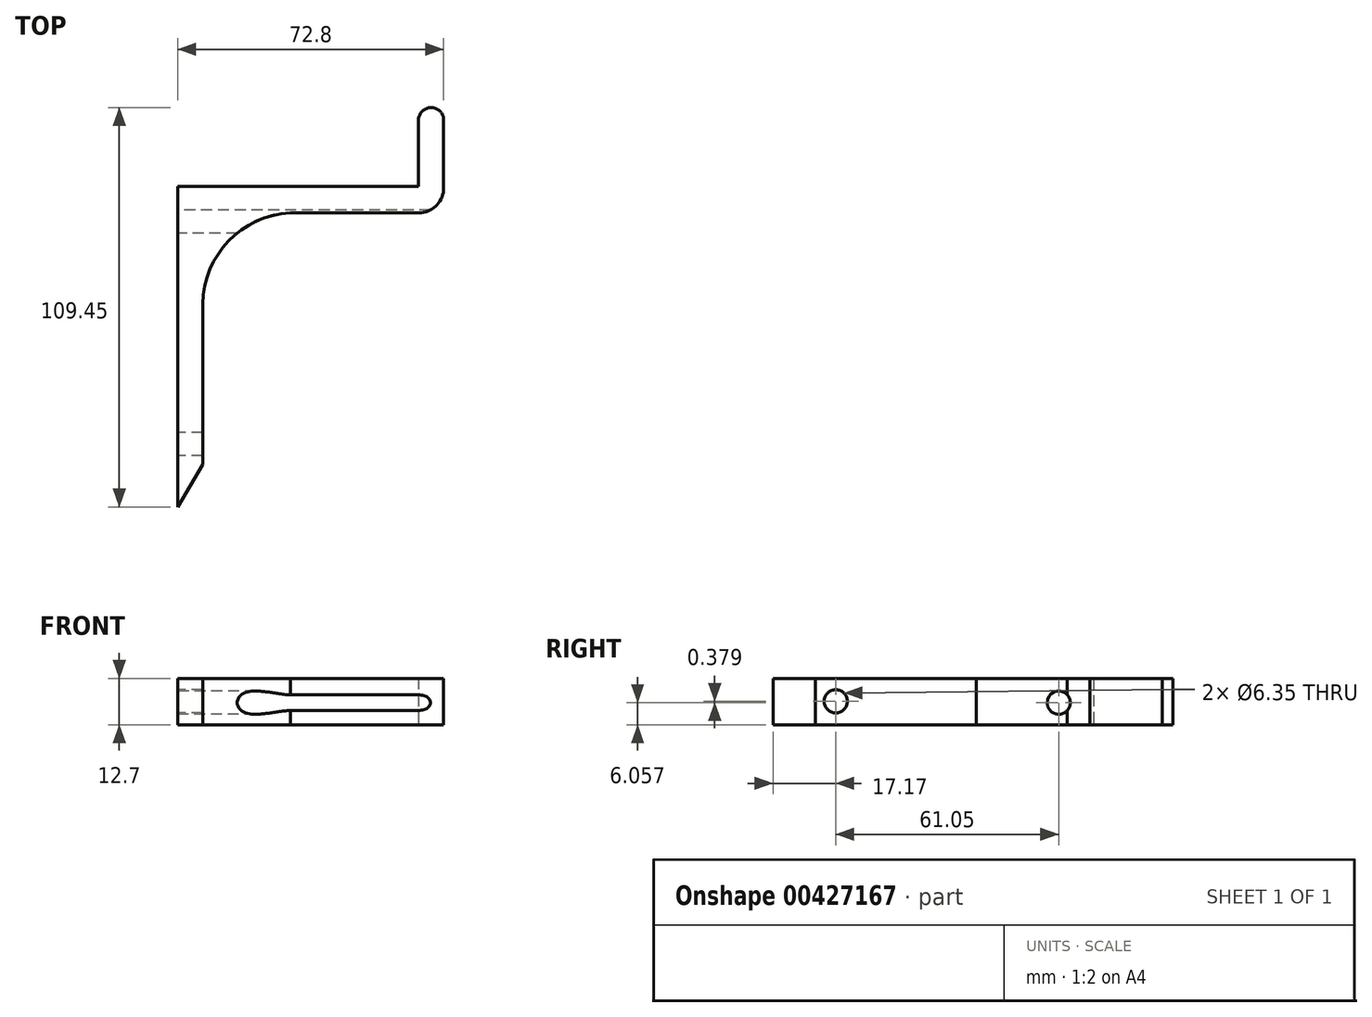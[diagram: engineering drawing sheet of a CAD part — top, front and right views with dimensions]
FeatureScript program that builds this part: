
annotation { "Feature Type Name" : "Feature", "Feature Type Description" : "" }
export const myFeature = defineFeature(function(context is Context, id is Id, definition is map)
    precondition{}
    {
        {
            var Q0;
            Q0=qCreatedBy(makeId("Top.planeOp"),FACE);
            var sketch = newSketch(context, id + "F0", { "sketchPlane" : qUnion([Q0])});
            skLineSegment(sketch, "E0.bottom", {"start": v(-64.27, 20.67) * mm, "end": v(-57.45, 20.67) * mm});
            skLineSegment(sketch, "E0.top", {"start": v(-64.27, -67.12) * mm, "end": v(-57.45, -67.12) * mm});
            skLineSegment(sketch, "E0.left", {"start": v(-64.27, 20.67) * mm, "end": v(-64.27, -67.12) * mm});
            skLineSegment(sketch, "E0.right", {"start": v(-57.45, -11.45) * mm, "end": v(-57.45, -67.12) * mm});
            skLineSegment(sketch, "E1.bottom", {"start": v(-57.45, 20.67) * mm, "end": v(1.7, 20.67) * mm});
            skLineSegment(sketch, "E1.top", {"start": v(-33.44, 13.46) * mm, "end": v(1.7, 13.46) * mm});
            skLineSegment(sketch, "E2.left", {"start": v(1.7, 20.67) * mm, "end": v(1.7, 39.44) * mm});
            skLineSegment(sketch, "E2.right", {"start": v(8.53, 19.7) * mm, "end": v(8.53, 39.44) * mm});
            skArc(sketch, "E3", {"start": v(-33.44, 13.46) * mm, "mid": v(-50.36, 5.75) * mm, "end": v(-57.45, -11.45) * mm});
            skArc(sketch, "E4", {"start": v(8.53, 39.44) * mm, "mid": v(5.12, 42.33) * mm, "end": v(1.7, 39.44) * mm});
            skArc(sketch, "E5", {"start": v(1.7, 13.46) * mm, "mid": v(6.33, 15.26) * mm, "end": v(8.53, 19.7) * mm});
            skSolve(sketch);
        }
        {
            var Q0;
            Q0=makeQuery(id+"F0.imprint","IMPRINT",FACE,{"disambiguationData":[TD([[makeQuery(id+"F0.imprint","IMPRINT",EDGE,{"derivedFrom":sQuery(id+"F0.wireOp",EDGE,"E0.bottom")}),-1.0]])]});
            extrude(context, id + "F1", {"entities" : qUnion([Q0]), "depth" : 12.7 * mm});
        }
        {
            var Q0;
            Q0=makeQuery(id+"F1.opExtrude","SWEPT_FACE",FACE,{"disambiguationData":[OSD([sQuery(id+"F0.wireOp",EDGE,"E0.left")])]});
            var sketch = newSketch(context, id + "F2", { "sketchPlane" : qUnion([Q0])});
            skCircle(sketch, "E6", {"center": v(-11.1, 6.06) * mm, "radius": 2.84 * mm});
            skCircle(sketch, "E7", {"center": v(49.95, 6.44) * mm, "radius": 3.09 * mm});
            skSolve(sketch);
        }
        {
            var Q0;
            Q0=sQuery(id+"F2.wireOp",VERTEX,"E6.center");
            var Q1;
            Q1=sQuery(id+"F2.wireOp",VERTEX,"E7.center");
            var Q2;
            Q2=makeQuery(id+"F1.opExtrude","SWEPT_BODY",BODY,{"disambiguationData":[OSD([sQuery(id+"F0.wireOp",EDGE,"E0.bottom"),sQuery(id+"F0.wireOp",EDGE,"E0.top"),sQuery(id+"F0.wireOp",EDGE,"E0.left"),sQuery(id+"F0.wireOp",EDGE,"E0.right"),sQuery(id+"F0.wireOp",EDGE,"E1.bottom"),sQuery(id+"F0.wireOp",EDGE,"E1.top"),sQuery(id+"F0.wireOp",EDGE,"E2.left"),sQuery(id+"F0.wireOp",EDGE,"E2.right"),sQuery(id+"F0.wireOp",EDGE,"E3"),sQuery(id+"F0.wireOp",EDGE,"E4"),sQuery(id+"F0.wireOp",EDGE,"E5")])]});
            hole(context, id + "F3", {"style" : HoleStyle.SIMPLE, "endStyle" : HoleEndStyle.THROUGH, "holeDiameter" : 6.35 * mm, "isTappedThrough" : true, "tappedDepth" : 12.7 * mm, "tapClearance" : 3, "locations" : qUnion([Q0, Q1]), "scope" : qUnion([Q2])});
        }
        {
            var Q0;
            Q0=makeQuery(id+"F1.opExtrude","CAP_FACE",FACE,{"disambiguationData":[OSD([sQuery(id+"F0.wireOp",EDGE,"E0.bottom"),sQuery(id+"F0.wireOp",EDGE,"E0.top"),sQuery(id+"F0.wireOp",EDGE,"E0.left"),sQuery(id+"F0.wireOp",EDGE,"E0.right"),sQuery(id+"F0.wireOp",EDGE,"E1.bottom"),sQuery(id+"F0.wireOp",EDGE,"E1.top"),sQuery(id+"F0.wireOp",EDGE,"E2.left"),sQuery(id+"F0.wireOp",EDGE,"E2.right"),sQuery(id+"F0.wireOp",EDGE,"E3"),sQuery(id+"F0.wireOp",EDGE,"E4"),sQuery(id+"F0.wireOp",EDGE,"E5")])],"isStart":true});
            var sketch = newSketch(context, id + "F4", { "sketchPlane" : qUnion([Q0])});
            skLineSegment(sketch, "E8", {"start": v(-64.27, 67.12) * mm, "end": v(-57.45, 55.51) * mm});
            skSolve(sketch);
        }
        {
            var Q0;
            {var subQ0=sQuery(id+"F4.wireOp",EDGE,"E8");Q0=makeQuery(id+"F4.imprint","IMPRINT",FACE,{"disambiguationData":[TD([[makeQuery(id+"F4.imprint","IMPRINT",EDGE,{"derivedFrom":subQ0}),1.0]])]});}
            extrude(context, id + "F5", {"entities" : qUnion([Q0]), "operationType" : NewBodyOperationType.REMOVE, "endBound" : BoundingType.THROUGH_ALL, "oppositeDirection" : true, "depth" : 25.4 * mm});
        }
    });
